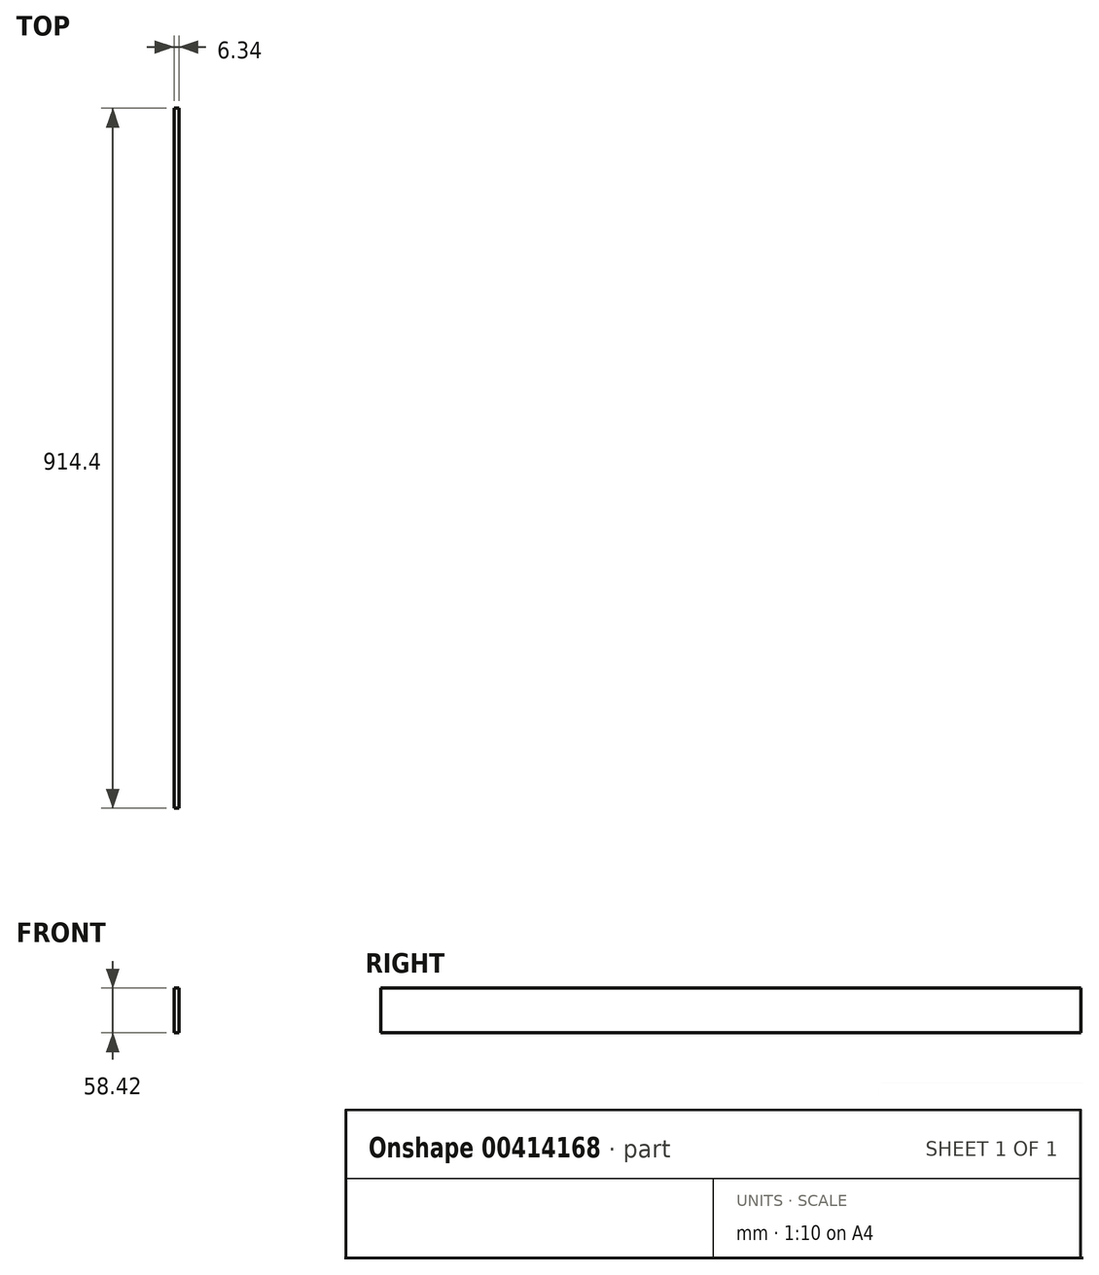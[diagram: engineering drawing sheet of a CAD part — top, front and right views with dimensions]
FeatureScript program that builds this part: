
annotation { "Feature Type Name" : "Feature", "Feature Type Description" : "" }
export const myFeature = defineFeature(function(context is Context, id is Id, definition is map)
    precondition{}
    {
        {
            var Q0;
            Q0=qCreatedBy(makeId("Front.planeOp"),FACE);
            var sketch = newSketch(context, id + "F0", { "sketchPlane" : qUnion([Q0])});
            skLineSegment(sketch, "E0.bottom", {"start": v(3.17, -29.21) * mm, "end": v(-3.18, -29.21) * mm});
            skLineSegment(sketch, "E0.top", {"start": v(3.18, 29.21) * mm, "end": v(-3.18, 29.21) * mm});
            skLineSegment(sketch, "E0.left", {"start": v(3.17, -29.21) * mm, "end": v(3.18, 29.2) * mm});
            skLineSegment(sketch, "E0.right", {"start": v(-3.18, -29.21) * mm, "end": v(-3.18, 29.2) * mm});
            skPoint(sketch, "E0.middle", {"position": v(0, 0) * mm});
            skSolve(sketch);
        }
        {
            var Q0;
            Q0 = qSketchRegion(id + "F0", true);
            extrude(context, id + "F1", {"entities" : qUnion([Q0]), "endBound" : BoundingType.SYMMETRIC, "depth" : 914.4 * mm});
        }
    });
